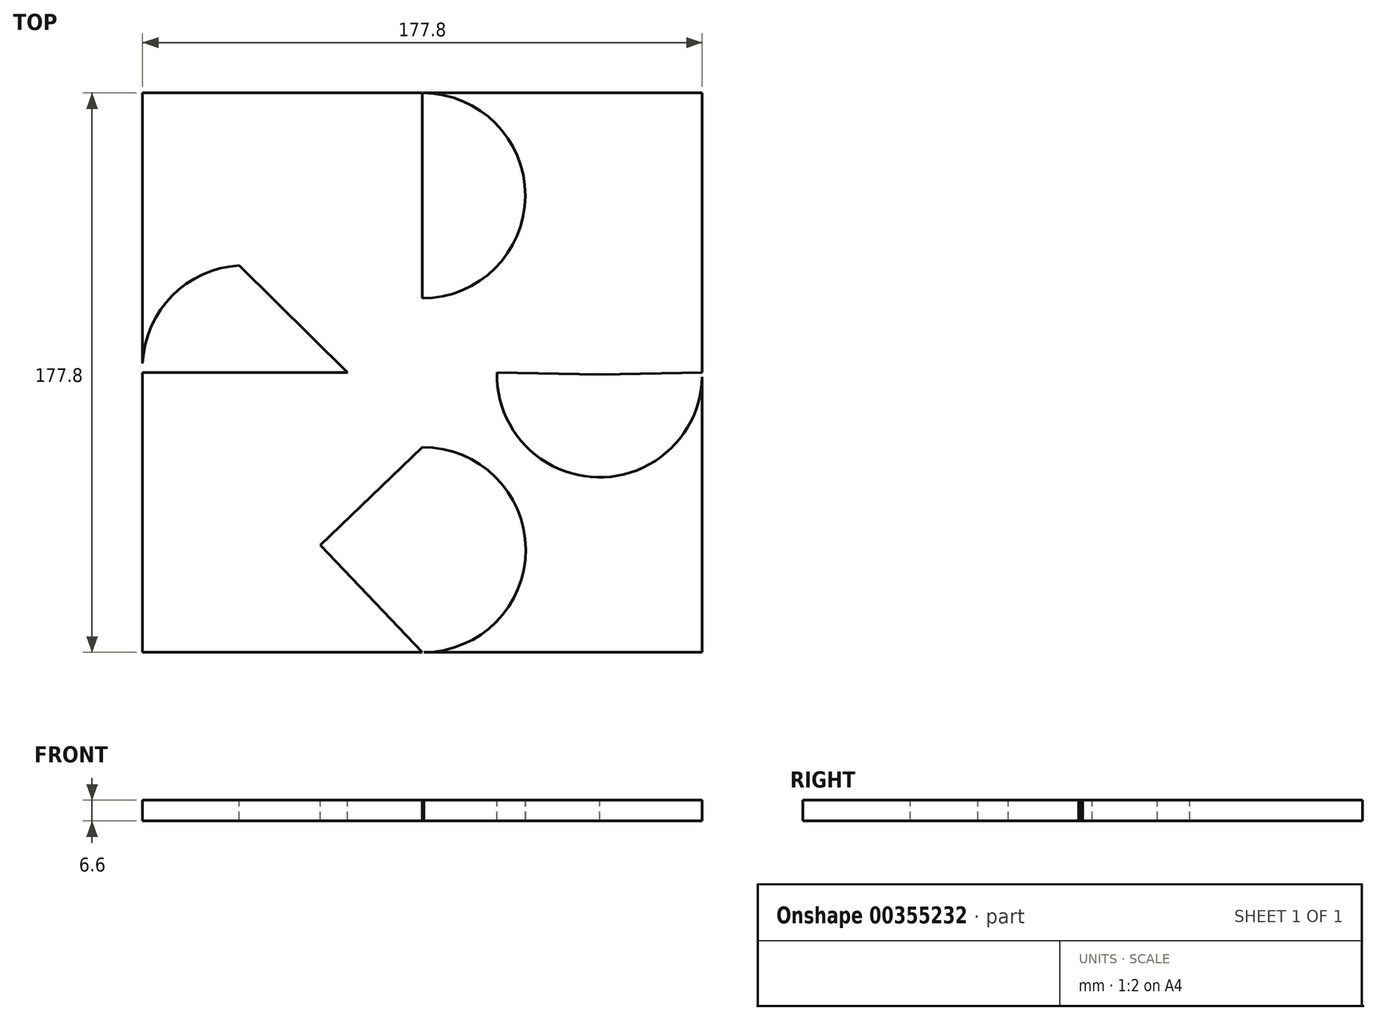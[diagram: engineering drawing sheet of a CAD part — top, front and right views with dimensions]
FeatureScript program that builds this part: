
annotation { "Feature Type Name" : "Feature", "Feature Type Description" : "" }
export const myFeature = defineFeature(function(context is Context, id is Id, definition is map)
    precondition{}
    {
        {
            var Q0;
            Q0=qCreatedBy(makeId("Top.planeOp"),FACE);
            var sketch = newSketch(context, id + "F0", { "sketchPlane" : qUnion([Q0])});
            skLineSegment(sketch, "E0.bottom", {"start": v(88.9, -88.9) * mm, "end": v(-88.9, -88.9) * mm});
            skLineSegment(sketch, "E0.top", {"start": v(88.9, 88.9) * mm, "end": v(-88.9, 88.9) * mm});
            skLineSegment(sketch, "E0.left", {"start": v(88.9, -88.9) * mm, "end": v(88.9, 88.9) * mm});
            skLineSegment(sketch, "E0.right", {"start": v(-88.9, -88.9) * mm, "end": v(-88.9, 88.9) * mm});
            skPoint(sketch, "E0.middle", {"position": v(0, 0) * mm});
            skLineSegment(sketch, "E1", {"start": v(-88.9, 88.9) * mm, "end": v(88.9, -88.9) * mm});
            skLineSegment(sketch, "E2", {"start": v(-88.9, -88.9) * mm, "end": v(88.9, 88.9) * mm});
            skCircle(sketch, "E3", {"center": v(-56.32, 1.5) * mm, "radius": 32.62 * mm});
            skPoint(sketch, "E3.first.point", {"position": v(-88.9, 0) * mm});
            skPoint(sketch, "E3.second.point", {"position": v(-23.74, 0) * mm});
            skPoint(sketch, "E3.second.point.positionSnap0", {"position": v(-88.9, 0) * mm});
            skPoint(sketch, "E3.third.point", {"position": v(-58.17, 34.07) * mm});
            skCircle(sketch, "E4", {"center": v(56.3, -0.65) * mm, "radius": 32.61 * mm});
            skPoint(sketch, "E4.first.point", {"position": v(88.9, 0) * mm});
            skPoint(sketch, "E4.second.point", {"position": v(23.69, 0) * mm});
            skPoint(sketch, "E4.second.point.positionSnap0", {"position": v(88.9, 0) * mm});
            skPoint(sketch, "E4.third.point", {"position": v(53.97, -33.18) * mm});
            skCircle(sketch, "E5", {"center": v(0.08, 56.29) * mm, "radius": 32.61 * mm});
            skPoint(sketch, "E5.first.point", {"position": v(0, 88.9) * mm});
            skPoint(sketch, "E5.second.point", {"position": v(0, 23.67) * mm});
            skPoint(sketch, "E5.second.point.positionSnap0", {"position": v(0, 88.9) * mm});
            skPoint(sketch, "E5.third.point", {"position": v(32.57, 59.17) * mm});
            skCircle(sketch, "E6", {"center": v(0.21, -56.29) * mm, "radius": 32.61 * mm});
            skPoint(sketch, "E6.first.point", {"position": v(0, -88.9) * mm});
            skPoint(sketch, "E6.second.point", {"position": v(0, -23.67) * mm});
            skPoint(sketch, "E6.second.point.positionSnap0", {"position": v(0, -88.9) * mm});
            skPoint(sketch, "E6.third.point", {"position": v(-32.37, -54.83) * mm});
            skLineSegment(sketch, "E7", {"start": v(-88.9, 0) * mm, "end": v(-58.17, 34.07) * mm});
            skLineSegment(sketch, "E8", {"start": v(-23.74, 0) * mm, "end": v(-58.17, 34.07) * mm});
            skLineSegment(sketch, "E9", {"start": v(-88.9, 0) * mm, "end": v(-23.74, 0) * mm});
            skLineSegment(sketch, "E10", {"start": v(23.69, 0) * mm, "end": v(56.3, -0.65) * mm});
            skLineSegment(sketch, "E11", {"start": v(23.69, 0) * mm, "end": v(53.97, -33.18) * mm});
            skLineSegment(sketch, "E12", {"start": v(53.97, -33.18) * mm, "end": v(88.9, 0) * mm});
            skLineSegment(sketch, "E13", {"start": v(88.9, 0) * mm, "end": v(56.3, -0.65) * mm});
            skLineSegment(sketch, "E14", {"start": v(32.57, 59.17) * mm, "end": v(0, 88.9) * mm});
            skLineSegment(sketch, "E15", {"start": v(0, 88.9) * mm, "end": v(0, 23.67) * mm});
            skLineSegment(sketch, "E16", {"start": v(0, 23.67) * mm, "end": v(32.57, 59.17) * mm});
            skLineSegment(sketch, "E17", {"start": v(0, -23.67) * mm, "end": v(0, -88.9) * mm});
            skLineSegment(sketch, "E18", {"start": v(0, -88.9) * mm, "end": v(-32.37, -54.83) * mm});
            skLineSegment(sketch, "E19", {"start": v(-32.37, -54.83) * mm, "end": v(0, -23.67) * mm});
            skSolve(sketch);
        }
        {
            var Q0;
            {var subQ1=sQuery(id+"F0.wireOp",EDGE,"E0.right");var subQ5=sQuery(id+"F0.wireOp",EDGE,"E3");var subQ6=makeQuery(id+"F0.imprint","INTERSECT",VERTEX,{"derivedFrom":[subQ1,subQ5]});Q0=makeQuery(id+"F0.imprint","IMPRINT",FACE,{"disambiguationData":[TD([[makeQuery(id+"F0.imprint","IMPRINT",EDGE,{"disambiguationData":[TD([[subQ6,-1.0]])],"derivedFrom":subQ1}),-1.0]])]});}
            var Q1;
            {var subQ1=sQuery(id+"F0.wireOp",EDGE,"E0.top");var subQ6=sQuery(id+"F0.wireOp",EDGE,"E5");var subQ7=makeQuery(id+"F0.imprint","INTERSECT",VERTEX,{"derivedFrom":[subQ1,subQ6]});Q1=makeQuery(id+"F0.imprint","IMPRINT",FACE,{"disambiguationData":[TD([[makeQuery(id+"F0.imprint","IMPRINT",EDGE,{"disambiguationData":[TD([[subQ7,1.0]])],"derivedFrom":subQ1}),1.0]])]});}
            var Q2;
            {var subQ1=sQuery(id+"F0.wireOp",EDGE,"E0.left");var subQ7=sQuery(id+"F0.wireOp",EDGE,"E4");var subQ9=makeQuery(id+"F0.imprint","INTERSECT",VERTEX,{"derivedFrom":[subQ1,subQ7]});Q2=makeQuery(id+"F0.imprint","IMPRINT",FACE,{"disambiguationData":[TD([[makeQuery(id+"F0.imprint","IMPRINT",EDGE,{"disambiguationData":[TD([[subQ9,1.0]])],"derivedFrom":subQ1}),1.0]])]});}
            var Q3;
            {var subQ1=sQuery(id+"F0.wireOp",EDGE,"E0.bottom");var subQ7=sQuery(id+"F0.wireOp",EDGE,"E6");var subQ10=makeQuery(id+"F0.imprint","INTERSECT",VERTEX,{"derivedFrom":[subQ1,subQ7]});Q3=makeQuery(id+"F0.imprint","IMPRINT",FACE,{"disambiguationData":[TD([[makeQuery(id+"F0.imprint","IMPRINT",EDGE,{"disambiguationData":[TD([[subQ10,1.0]])],"derivedFrom":subQ1}),-1.0]])]});}
            var Q4;
            {var subQ0=sQuery(id+"F0.wireOp",EDGE,"E10");Q4=makeQuery(id+"F0.imprint","IMPRINT",FACE,{"disambiguationData":[TD([[makeQuery(id+"F0.imprint","IMPRINT",EDGE,{"derivedFrom":subQ0}),1.0]])]});}
            var Q5;
            {var subQ0=sQuery(id+"F0.wireOp",EDGE,"E15");Q5=makeQuery(id+"F0.imprint","IMPRINT",FACE,{"disambiguationData":[TD([[makeQuery(id+"F0.imprint","IMPRINT",EDGE,{"derivedFrom":subQ0}),-1.0]])]});}
            var Q6;
            {var subQ0=sQuery(id+"F0.wireOp",EDGE,"E9");Q6=makeQuery(id+"F0.imprint","IMPRINT",FACE,{"disambiguationData":[TD([[makeQuery(id+"F0.imprint","IMPRINT",EDGE,{"derivedFrom":subQ0}),-1.0]])]});}
            var Q7;
            {var subQ0=sQuery(id+"F0.wireOp",EDGE,"E18");Q7=makeQuery(id+"F0.imprint","IMPRINT",FACE,{"disambiguationData":[TD([[makeQuery(id+"F0.imprint","IMPRINT",EDGE,{"derivedFrom":subQ0}),1.0]])]});}
            var Q8;
            {var subQ0=sQuery(id+"F0.wireOp",EDGE,"E19");Q8=makeQuery(id+"F0.imprint","IMPRINT",FACE,{"disambiguationData":[TD([[makeQuery(id+"F0.imprint","IMPRINT",EDGE,{"derivedFrom":subQ0}),1.0]])]});}
            var Q9;
            {var subQ0=sQuery(id+"F0.wireOp",EDGE,"E8");Q9=makeQuery(id+"F0.imprint","IMPRINT",FACE,{"disambiguationData":[TD([[makeQuery(id+"F0.imprint","IMPRINT",EDGE,{"derivedFrom":subQ0}),-1.0]])]});}
            extrude(context, id + "F1", {"entities" : qUnion([Q0, Q1, Q2, Q3, Q4, Q5, Q6, Q7, Q8, Q9]), "oppositeDirection" : true, "depth" : 6.6 * mm});
        }
    });
